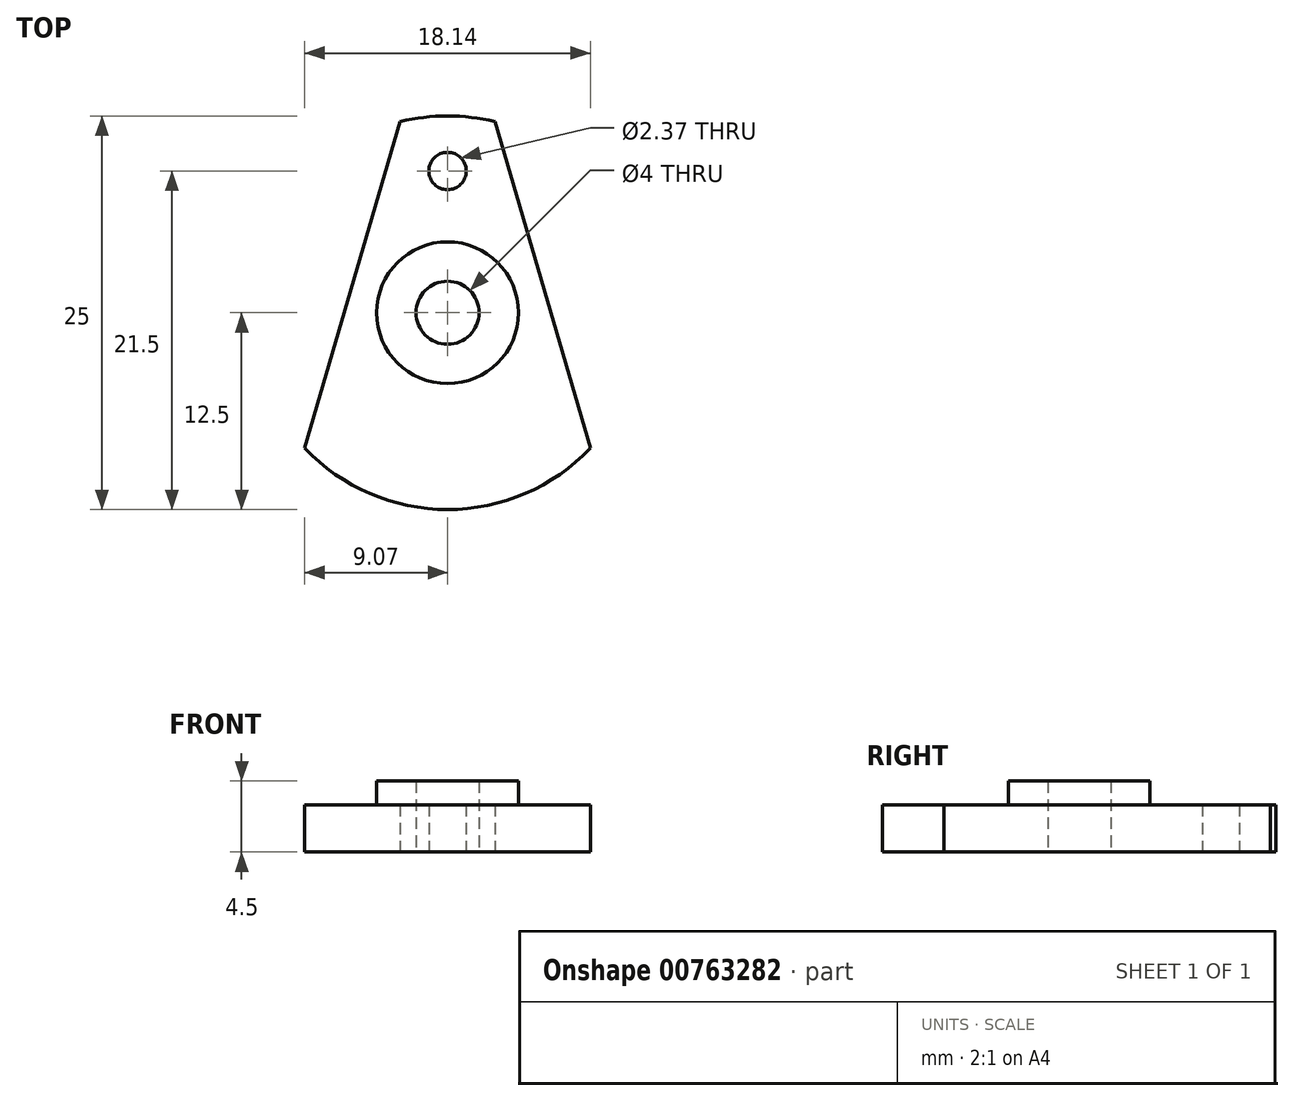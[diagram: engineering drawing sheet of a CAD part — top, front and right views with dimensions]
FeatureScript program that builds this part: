
annotation { "Feature Type Name" : "Feature", "Feature Type Description" : "" }
export const myFeature = defineFeature(function(context is Context, id is Id, definition is map)
    precondition{}
    {
        {
            var Q0;
            Q0=qCreatedBy(makeId("Top.planeOp"),FACE);
            var sketch = newSketch(context, id + "F0", { "sketchPlane" : qUnion([Q0])});
            skArc(sketch, "E0", {"start": v(-9.07, -8.6) * mm, "mid": v(0, -12.5) * mm, "end": v(9.07, -8.6) * mm});
            skLineSegment(sketch, "E1", {"start": v(3, 12.13) * mm, "end": v(9.07, -8.6) * mm});
            skLineSegment(sketch, "E2.MirrorCS", {"start": v(-3, 12.13) * mm, "end": v(-9.07, -8.6) * mm});
            skArc(sketch, "E3.trimOffspring", {"start": v(3, 12.13) * mm, "mid": v(0, 12.5) * mm, "end": v(-3, 12.13) * mm});
            skPoint(sketch, "E4.start.orphan", {"position": v(0, 25.64) * mm});
            skCircle(sketch, "E5", {"center": v(0, 0) * mm, "radius": 4.5 * mm});
            skCircle(sketch, "E6", {"center": v(0, 9) * mm, "radius": 1.19 * mm});
            skCircle(sketch, "E7", {"center": v(0, 0) * mm, "radius": 2 * mm});
            skSolve(sketch);
        }
        {
            var Q0;
            Q0=makeQuery(id+"F0.imprint","IMPRINT",FACE,{"disambiguationData":[TD([[makeQuery(id+"F0.imprint","IMPRINT",EDGE,{"derivedFrom":sQuery(id+"F0.wireOp",EDGE,"E0")}),1.0]])]});
            extrude(context, id + "F1", {"entities" : qUnion([Q0]), "depth" : 3 * mm, "offsetDistance" : 25 * mm});
        }
        {
            var Q0;
            Q0=makeQuery(id+"F0.imprint","IMPRINT",FACE,{"disambiguationData":[TD([[makeQuery(id+"F0.imprint","IMPRINT",EDGE,{"derivedFrom":sQuery(id+"F0.wireOp",EDGE,"E5")}),1.0]])]});
            extrude(context, id + "F2", {"entities" : qUnion([Q0]), "operationType" : NewBodyOperationType.ADD, "depth" : 4.5 * mm, "offsetDistance" : 25 * mm});
        }
    });
